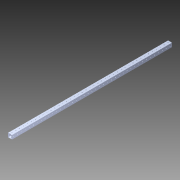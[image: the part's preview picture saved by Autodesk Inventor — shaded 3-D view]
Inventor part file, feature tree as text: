
AUTODESK INVENTOR PART (.ipt)
format: ipt  version: 2014 SP1 (Build 180222100, 222)  size: 1,661,952 bytes
history: native  units: in
note: dims shown in document units (in); Inventor stores cm internally (conversion verified against a paired STEP export)
features: extrude x2, sketch x2, pattern_circular x1, other x1, mirror x1, imported_body x1
ambient origin geometry x8: Origin, YZ Plane, XZ Plane, XY Plane, X Axis, Y Axis, Z Axis, Center Point
bodies: Body1 (feature_tree)
feature tree (8):
  pattern_circular  "CirPattern2"
  other  "1x1 tube1"
  extrude  "Extrusion1"  Depth=1.0in TaperAngle=0.0deg
  mirror  "Mirror1"
  extrude  "Extrusion2"  [1 undecoded]
  imported_body  "Base1"
  sketch  "Sketch1"  dims[d0=38.0in d1=0.0in d2=1.0in d3=0.0in]
  sketch  "Sketch3"
note: 1 required parameter value undecoded (feature->parameter linkage not recoverable at this tier; creation-order binding heuristic only, values carry confidence <= 0.55)
